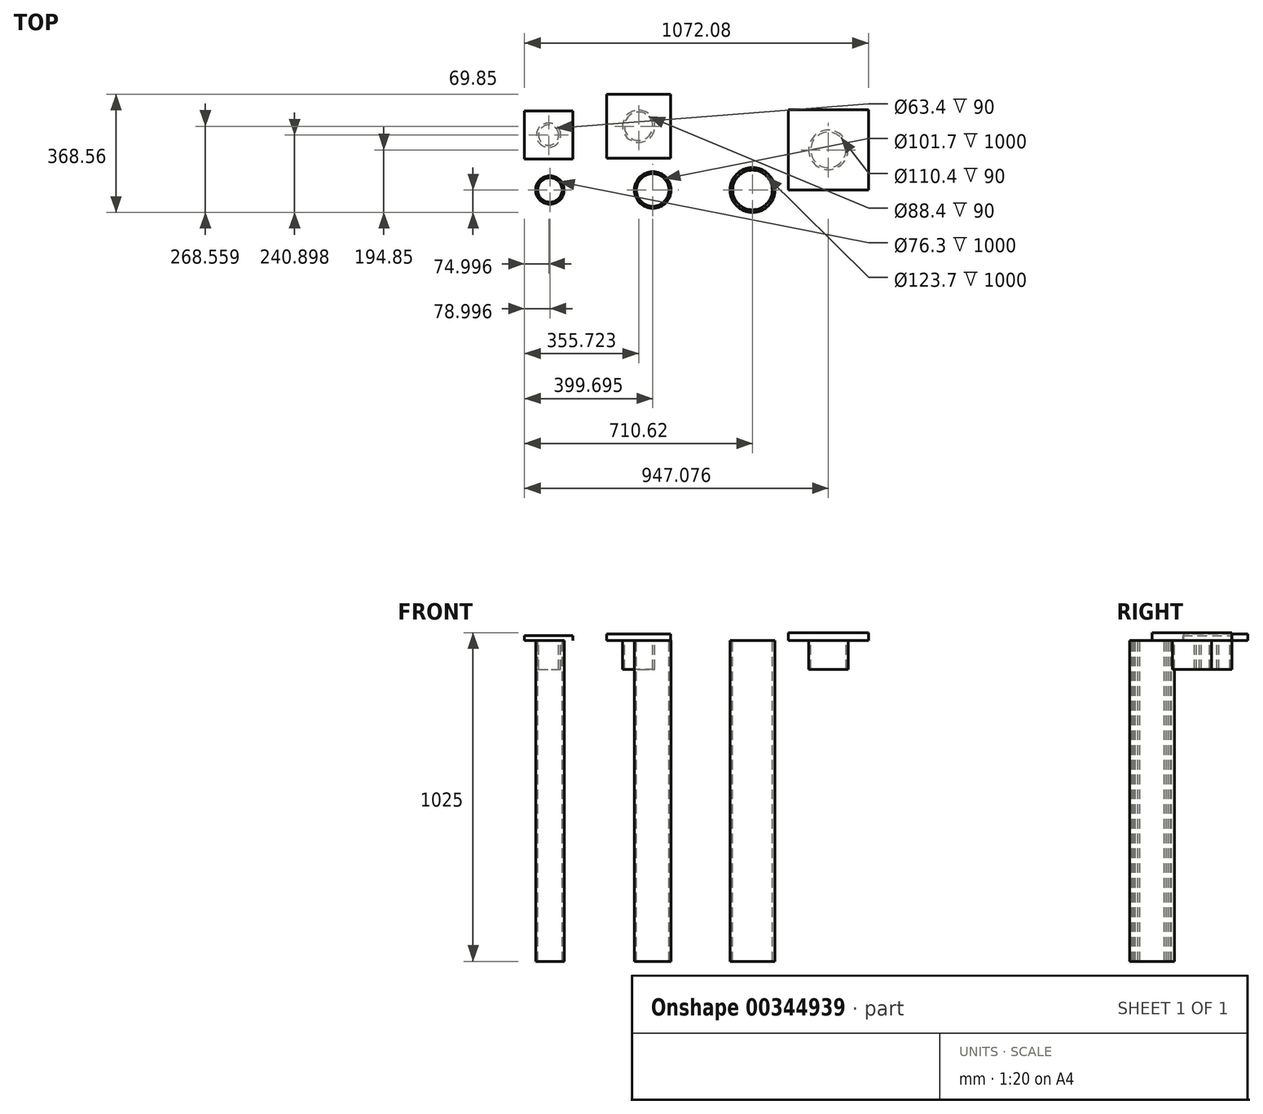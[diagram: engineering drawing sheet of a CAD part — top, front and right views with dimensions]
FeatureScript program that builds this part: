
annotation { "Feature Type Name" : "Feature", "Feature Type Description" : "" }
export const myFeature = defineFeature(function(context is Context, id is Id, definition is map)
    precondition{}
    {
        {
            var Q0;
            Q0=qCreatedBy(makeId("Top.planeOp"),FACE);
            var sketch = newSketch(context, id + "F0", { "sketchPlane" : qUnion([Q0])});
            skCircle(sketch, "E0", {"center": v(0, 0) * mm, "radius": 69.85 * mm});
            skCircle(sketch, "E1", {"center": v(0, 0) * mm, "radius": 61.85 * mm});
            skSolve(sketch);
        }
        {
            var Q0;
            Q0=makeQuery(id+"F0.imprint","IMPRINT",FACE,{"disambiguationData":[TD([[makeQuery(id+"F0.imprint","IMPRINT",EDGE,{"derivedFrom":sQuery(id+"F0.wireOp",EDGE,"E0")}),1.0]])]});
            extrude(context, id + "F1", {"entities" : qUnion([Q0]), "oppositeDirection" : true, "depth" : 1000 * mm});
        }
        {
            var Q0;
            Q0=qCreatedBy(makeId("Top.planeOp"),FACE);
            var sketch = newSketch(context, id + "F2", { "sketchPlane" : qUnion([Q0])});
            skLineSegment(sketch, "E2.bottom", {"start": v(111.46, 250) * mm, "end": v(361.46, 250) * mm});
            skLineSegment(sketch, "E2.top", {"start": v(111.46, 0) * mm, "end": v(361.46, 0) * mm});
            skLineSegment(sketch, "E2.left", {"start": v(111.46, 250) * mm, "end": v(111.46, 0) * mm});
            skLineSegment(sketch, "E2.right", {"start": v(361.46, 250) * mm, "end": v(361.46, 0) * mm});
            skSolve(sketch);
        }
        {
            var Q0;
            Q0=makeQuery(id+"F2.imprint","IMPRINT",FACE,{"disambiguationData":[TD([[makeQuery(id+"F2.imprint","IMPRINT",EDGE,{"derivedFrom":sQuery(id+"F2.wireOp",EDGE,"E2.bottom")}),-1.0]])]});
            extrude(context, id + "F3", {"entities" : qUnion([Q0]), "depth" : 25 * mm});
        }
        {
            var Q0;
            Q0=qCreatedBy(makeId("Top.planeOp"),FACE);
            var sketch = newSketch(context, id + "F4", { "sketchPlane" : qUnion([Q0])});
            skCircle(sketch, "E3", {"center": v(-310.92, 0) * mm, "radius": 57.15 * mm});
            skCircle(sketch, "E4", {"center": v(-310.92, 0) * mm, "radius": 50.85 * mm});
            skSolve(sketch);
        }
        {
            var Q0;
            Q0=makeQuery(id+"F4.imprint","IMPRINT",FACE,{"disambiguationData":[TD([[makeQuery(id+"F4.imprint","IMPRINT",EDGE,{"derivedFrom":sQuery(id+"F4.wireOp",EDGE,"E3")}),1.0]])]});
            extrude(context, id + "F5", {"entities" : qUnion([Q0]), "oppositeDirection" : true, "depth" : 1000 * mm});
        }
        {
            var Q0;
            Q0=qCreatedBy(makeId("Top.planeOp"),FACE);
            var sketch = newSketch(context, id + "F6", { "sketchPlane" : qUnion([Q0])});
            skLineSegment(sketch, "E5.bottom", {"start": v(-454.9, 298.7) * mm, "end": v(-254.9, 298.7) * mm});
            skLineSegment(sketch, "E5.top", {"start": v(-454.9, 98.7) * mm, "end": v(-254.9, 98.7) * mm});
            skLineSegment(sketch, "E5.left", {"start": v(-454.9, 298.7) * mm, "end": v(-454.9, 98.7) * mm});
            skLineSegment(sketch, "E5.right", {"start": v(-254.9, 298.7) * mm, "end": v(-254.9, 98.7) * mm});
            skSolve(sketch);
        }
        {
            var Q0;
            Q0=makeQuery(id+"F6.imprint","IMPRINT",FACE,{"disambiguationData":[TD([[makeQuery(id+"F6.imprint","IMPRINT",EDGE,{"derivedFrom":sQuery(id+"F6.wireOp",EDGE,"E5.bottom")}),-1.0]])]});
            extrude(context, id + "F7", {"entities" : qUnion([Q0]), "depth" : 20 * mm});
        }
        {
            var Q0;
            Q0=makeQuery(id+"F7.opExtrude","CAP_FACE",FACE,{"disambiguationData":[OSD([sQuery(id+"F6.wireOp",EDGE,"E5.bottom"),sQuery(id+"F6.wireOp",EDGE,"E5.top"),sQuery(id+"F6.wireOp",EDGE,"E5.left"),sQuery(id+"F6.wireOp",EDGE,"E5.right")])],"isStart":true});
            var sketch = newSketch(context, id + "F8", { "sketchPlane" : qUnion([Q0])});
            skCircle(sketch, "E6", {"center": v(-354.9, -198.7) * mm, "radius": 50.5 * mm});
            skCircle(sketch, "E7", {"center": v(-354.9, -198.7) * mm, "radius": 44.2 * mm});
            skSolve(sketch);
        }
        {
            var Q0;
            Q0=makeQuery(id+"F8.imprint","IMPRINT",FACE,{"disambiguationData":[TD([[makeQuery(id+"F8.imprint","IMPRINT",EDGE,{"derivedFrom":sQuery(id+"F8.wireOp",EDGE,"E6")}),1.0]])]});
            var Q1;
            Q1=sQuery(id+"F8.wireOp",EDGE,"E6");
            extrude(context, id + "F9", {"entities" : qUnion([Q0]), "operationType" : NewBodyOperationType.ADD, "surfaceEntities" : qUnion([Q1]), "depth" : 90 * mm});
        }
        {
            var Q0;
            Q0=makeQuery(id+"F3.opExtrude","CAP_FACE",FACE,{"disambiguationData":[OSD([sQuery(id+"F2.wireOp",EDGE,"E2.bottom"),sQuery(id+"F2.wireOp",EDGE,"E2.top"),sQuery(id+"F2.wireOp",EDGE,"E2.left"),sQuery(id+"F2.wireOp",EDGE,"E2.right")])],"isStart":true});
            var sketch = newSketch(context, id + "F10", { "sketchPlane" : qUnion([Q0])});
            skCircle(sketch, "E8", {"center": v(236.46, -125) * mm, "radius": 61.5 * mm});
            skPoint(sketch, "E8.centerSnap0", {"position": v(236.46, -250) * mm});
            skPoint(sketch, "E8.centerSnap1", {"position": v(361.46, -125) * mm});
            skCircle(sketch, "E9", {"center": v(236.46, -125) * mm, "radius": 55.2 * mm});
            skSolve(sketch);
        }
        {
            var Q0;
            Q0=makeQuery(id+"F10.imprint","IMPRINT",FACE,{"disambiguationData":[TD([[makeQuery(id+"F10.imprint","IMPRINT",EDGE,{"derivedFrom":sQuery(id+"F10.wireOp",EDGE,"E8")}),1.0]])]});
            extrude(context, id + "F11", {"entities" : qUnion([Q0]), "operationType" : NewBodyOperationType.ADD, "depth" : 90 * mm});
        }
        {
            var Q0;
            Q0=qCreatedBy(makeId("Top.planeOp"),FACE);
            var sketch = newSketch(context, id + "F12", { "sketchPlane" : qUnion([Q0])});
            skCircle(sketch, "E10", {"center": v(-631.62, 0) * mm, "radius": 44.45 * mm});
            skCircle(sketch, "E11", {"center": v(-631.62, 0) * mm, "radius": 38.15 * mm});
            skSolve(sketch);
        }
        {
            var Q0;
            Q0=makeQuery(id+"F12.imprint","IMPRINT",FACE,{"disambiguationData":[TD([[makeQuery(id+"F12.imprint","IMPRINT",EDGE,{"derivedFrom":sQuery(id+"F12.wireOp",EDGE,"E10")}),1.0]])]});
            extrude(context, id + "F13", {"entities" : qUnion([Q0]), "oppositeDirection" : true, "depth" : 1000 * mm});
        }
        {
            var Q0;
            Q0=qCreatedBy(makeId("Top.planeOp"),FACE);
            var sketch = newSketch(context, id + "F14", { "sketchPlane" : qUnion([Q0])});
            skLineSegment(sketch, "E12.bottom", {"start": v(-710.62, 96.05) * mm, "end": v(-560.62, 96.05) * mm});
            skLineSegment(sketch, "E12.top", {"start": v(-710.62, 246.05) * mm, "end": v(-560.62, 246.05) * mm});
            skLineSegment(sketch, "E12.left", {"start": v(-710.62, 96.05) * mm, "end": v(-710.62, 246.05) * mm});
            skLineSegment(sketch, "E12.right", {"start": v(-560.62, 96.05) * mm, "end": v(-560.62, 246.05) * mm});
            skSolve(sketch);
        }
        {
            var Q0;
            Q0=makeQuery(id+"F14.imprint","IMPRINT",FACE,{"disambiguationData":[TD([[makeQuery(id+"F14.imprint","IMPRINT",EDGE,{"derivedFrom":sQuery(id+"F14.wireOp",EDGE,"E12.bottom")}),1.0]])]});
            extrude(context, id + "F15", {"entities" : qUnion([Q0]), "depth" : 15 * mm});
        }
        {
            var Q0;
            Q0=makeQuery(id+"F15.opExtrude","CAP_FACE",FACE,{"disambiguationData":[OSD([sQuery(id+"F14.wireOp",EDGE,"E12.bottom"),sQuery(id+"F14.wireOp",EDGE,"E12.top"),sQuery(id+"F14.wireOp",EDGE,"E12.left"),sQuery(id+"F14.wireOp",EDGE,"E12.right")])],"isStart":true});
            var sketch = newSketch(context, id + "F16", { "sketchPlane" : qUnion([Q0])});
            skCircle(sketch, "E13", {"center": v(-635.62, -171.05) * mm, "radius": 38 * mm});
            skPoint(sketch, "E13.centerSnap0", {"position": v(-635.62, -96.05) * mm});
            skCircle(sketch, "E14", {"center": v(-635.62, -171.05) * mm, "radius": 31.7 * mm});
            skSolve(sketch);
        }
        {
            var Q0;
            Q0=makeQuery(id+"F16.imprint","IMPRINT",FACE,{"disambiguationData":[TD([[makeQuery(id+"F16.imprint","IMPRINT",EDGE,{"derivedFrom":sQuery(id+"F16.wireOp",EDGE,"E13")}),1.0]])]});
            extrude(context, id + "F17", {"entities" : qUnion([Q0]), "operationType" : NewBodyOperationType.ADD, "depth" : 90 * mm});
        }
    });
